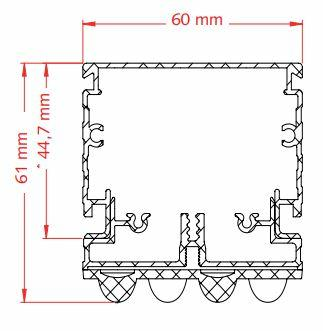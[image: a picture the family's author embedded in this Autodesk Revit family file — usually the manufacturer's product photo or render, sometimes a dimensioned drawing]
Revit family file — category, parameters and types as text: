
# Revit family: Rowan 1530mm
name_source: partatom
category: Lighting Fixtures
revit_build: Autodesk Revit 2017 (Build: 20190508_0315(x64)
units: mm (PartAtom-declared; Revit-internal decimal feet)

## family parameters
Always vertical = No
Cut with Voids When Loaded = No
Light Source = No
Part Type = Normal
Room Calculation Point = No
Round Connector Dimension = Use Diameter
Shared = No
Work Plane-Based = No

## types (3) — shared parameters
Article Number = On Request
Assembly Code = 63.0
Description = Veko Lightline
IK Value = IK02
IP Value = IP20
IfcExportAs = IfcLightFixtureType
IfcExportType = POINTSOURCE
Lamp = LED
Manufacturer = Veko Lightsystems
URL = https://www.veko.com
Wattage Comments = Load can vary between 10,3 - 154,5(W)

## per-type parameters (varying)
| type | Apparent Load | Model | Selected Optic |
| Narrow | 10 VA | Rowan Narrow | Optics Rowan 1530 : Narrow |
| Semi Wide | 11 VA | Rowan Semi Wide | Optics Rowan 1530 : Semi Wide |
| Wide | 11 VA | Rowan Wide | Optics Rowan 1530 : Wide |

## geometry (parser evidence)
native form markers: Sweep x54
no freeform markers — native parametric forms only
